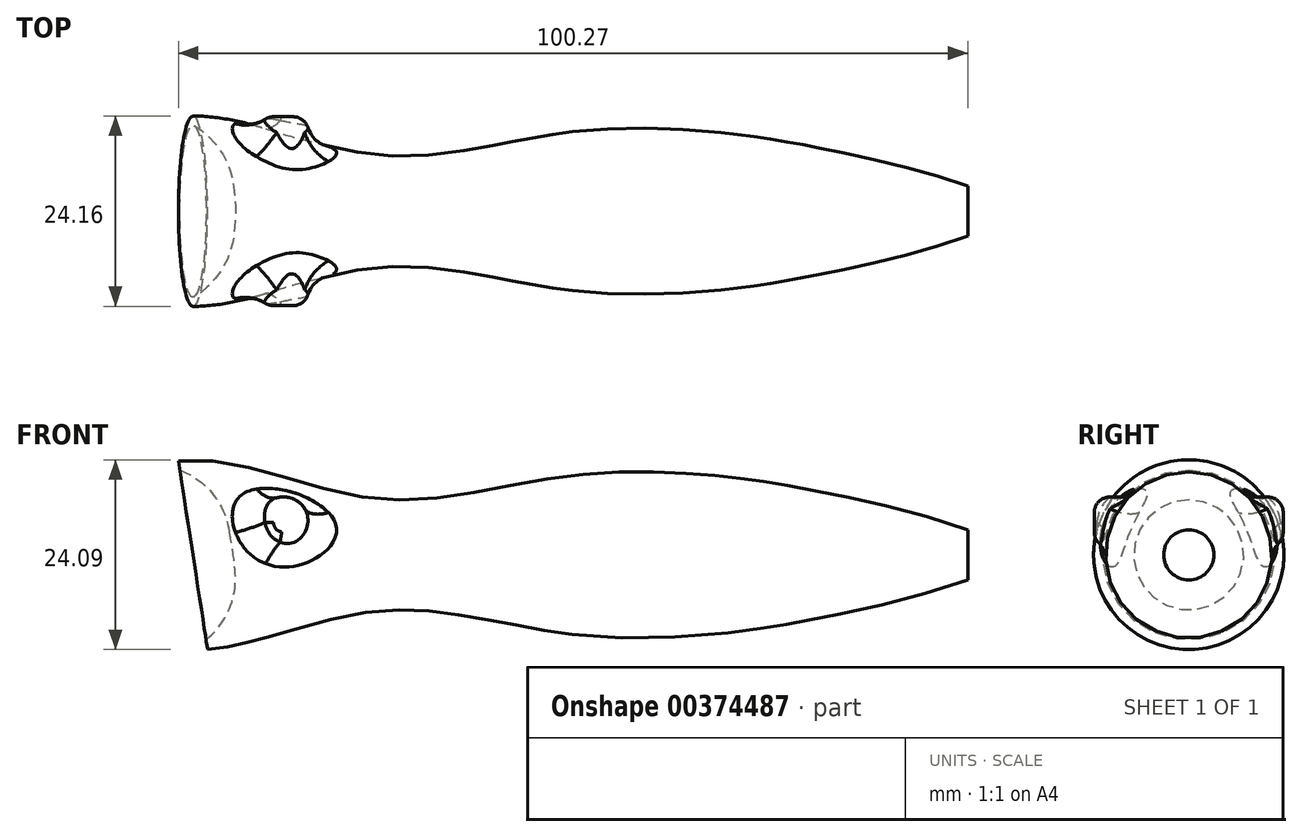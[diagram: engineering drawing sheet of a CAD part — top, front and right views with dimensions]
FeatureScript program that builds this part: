
annotation { "Feature Type Name" : "Feature", "Feature Type Description" : "" }
export const myFeature = defineFeature(function(context is Context, id is Id, definition is map)
    precondition{}
    {
        {
            var Q0;
            Q0=qCreatedBy(makeId("Front.planeOp"),FACE);
            var sketch = newSketch(context, id + "F0", { "sketchPlane" : qUnion([Q0])});
            skLineSegment(sketch, "E0", {"start": v(-64.17, 0) * mm, "end": v(44.05, 0) * mm});
            skFitSpline(sketch, "E1", {"points": [v(-64.13, 11.91) * mm, v(-39.28, 7.2) * mm, v(-14.5, 10.01) * mm, v(5.16, 9.98) * mm, v(16.36, 8.27) * mm, v(44.05, 0) * mm], "startDerivative": vector(102.28, 15.68) * mm, "endDerivative": vector(118.61, -59.18) * mm});
            skLineSegment(sketch, "E2.bottom", {"start": v(36.42, 9.8) * mm, "end": v(56.27, 9.8) * mm});
            skLineSegment(sketch, "E2.top", {"start": v(36.42, -4.91) * mm, "end": v(56.27, -4.91) * mm});
            skLineSegment(sketch, "E2.left", {"start": v(36.42, 9.8) * mm, "end": v(36.42, -4.91) * mm});
            skLineSegment(sketch, "E2.right", {"start": v(56.27, 9.8) * mm, "end": v(56.27, -4.91) * mm});
            skLineSegment(sketch, "E3", {"start": v(-64.13, 11.91) * mm, "end": v(-64.17, 0) * mm});
            skSolve(sketch);
        }
        {
            var Q0;
            {var subQ0=sQuery(id+"F0.wireOp",EDGE,"E3");Q0=makeQuery(id+"F0.imprint","IMPRINT",FACE,{"disambiguationData":[TD([[makeQuery(id+"F0.imprint","IMPRINT",EDGE,{"derivedFrom":subQ0}),1.0]])]});}
            var Q1;
            Q1=sQuery(id+"F0.wireOp",EDGE,"E0");
            revolve(context, id + "F1", {"entities" : qUnion([Q0]), "axis" : qUnion([Q1]), "revolveType" : RevolveType.FULL});
        }
        {
            var Q0;
            Q0=qCreatedBy(makeId("Front.planeOp"),FACE);
            var sketch = newSketch(context, id + "F2", { "sketchPlane" : qUnion([Q0])});
            skLineSegment(sketch, "E4", {"start": v(-65.45, 22.3) * mm, "end": v(-56.64, -34.7) * mm});
            skLineSegment(sketch, "E5", {"start": v(-56.64, -34.7) * mm, "end": v(-81.8, -34.7) * mm});
            skLineSegment(sketch, "E6", {"start": v(-81.8, -34.7) * mm, "end": v(-65.45, 22.3) * mm});
            skSolve(sketch);
        }
        {
            var Q0;
            Q0=makeQuery(id+"F2.imprint","IMPRINT",FACE,{"disambiguationData":[TD([[makeQuery(id+"F2.imprint","IMPRINT",EDGE,{"derivedFrom":sQuery(id+"F2.wireOp",EDGE,"E4")}),-1.0]])]});
            extrude(context, id + "F3", {"entities" : qUnion([Q0]), "operationType" : NewBodyOperationType.REMOVE, "endBound" : BoundingType.SYMMETRIC, "oppositeDirection" : true, "depth" : 32.6 * mm});
        }
        {
            var Q0;
            Q0=makeQuery(id+"F3.boolean.opBoolean","COPY",FACE,{"derivedFrom":makeQuery(id+"F3.opExtrude","SWEPT_FACE",FACE,{"disambiguationData":[OSD([sQuery(id+"F2.wireOp",EDGE,"E4")])]})});
            var sketch = newSketch(context, id + "F4", { "sketchPlane" : qUnion([Q0])});
            skCircle(sketch, "E7", {"center": v(0, 9.47) * mm, "radius": 10.92 * mm});
            skSolve(sketch);
        }
        {
            var Q0;
            Q0 = qSketchRegion(id + "F4", true);
            extrude(context, id + "F5", {"entities" : qUnion([Q0]), "operationType" : NewBodyOperationType.REMOVE, "oppositeDirection" : true, "depth" : 5 * mm});
        }
        {
            var Q0;
            Q0=makeQuery(id+"F5.boolean.opBoolean","COPY",EDGE,{"derivedFrom":makeQuery(id+"F5.opExtrude","CAP_EDGE",EDGE,{"disambiguationData":[OSD([sQuery(id+"F4.wireOp",EDGE,"E7")])],"isStart":false})});
            fillet(context, id + "F6", {"entities" : qUnion([Q0]), "radius" : 10 * mm, "tangentPropagation" : true, "allowEdgeOverflow" : false});
        }
        {
            var Q0;
            Q0=qCreatedBy(makeId("Front.planeOp"),FACE);
            var sketch = newSketch(context, id + "F7", { "sketchPlane" : qUnion([Q0])});
            skCircle(sketch, "E8", {"center": v(-50.52, 4.14) * mm, "radius": 3.23 * mm});
            skSolve(sketch);
        }
        {
            var Q0;
            Q0 = qSketchRegion(id + "F7", true);
            extrude(context, id + "F8", {"entities" : qUnion([Q0]), "operationType" : NewBodyOperationType.ADD, "endBound" : BoundingType.SYMMETRIC, "oppositeDirection" : true, "depth" : 24 * mm});
        }
        {
            var Q0;
            Q0=makeQuery(id+"F8.opExtrude","CAP_EDGE",EDGE,{"disambiguationData":[OSD([sQuery(id+"F7.wireOp",EDGE,"E8")])],"isStart":true});
            var Q1;
            Q1=makeQuery(id+"F8.opExtrude","CAP_EDGE",EDGE,{"disambiguationData":[OSD([sQuery(id+"F7.wireOp",EDGE,"E8")])],"isStart":false});
            fillet(context, id + "F9", {"entities" : qUnion([Q0, Q1]), "radius" : 2 * mm, "tangentPropagation" : true, "allowEdgeOverflow" : false});
        }
        {
            var Q0;
            Q0=makeQuery(id+"F8.boolean.opBoolean","INTERSECT",EDGE,{"disambiguationData":[OD(0.0)],"derivedFrom":[makeQuery(id+"F1.opRevolve","SWEPT_FACE",FACE,{"disambiguationData":[OSD([sQuery(id+"F0.wireOp",EDGE,"E1")])]}),makeQuery(id+"F8.opExtrude","SWEPT_FACE",FACE,{"disambiguationData":[OSD([sQuery(id+"F7.wireOp",EDGE,"E8")])]})]});
            var Q1;
            Q1=makeQuery(id+"F8.boolean.opBoolean","INTERSECT",EDGE,{"disambiguationData":[OD(1.0)],"derivedFrom":[makeQuery(id+"F1.opRevolve","SWEPT_FACE",FACE,{"disambiguationData":[OSD([sQuery(id+"F0.wireOp",EDGE,"E1")])]}),makeQuery(id+"F8.opExtrude","SWEPT_FACE",FACE,{"disambiguationData":[OSD([sQuery(id+"F7.wireOp",EDGE,"E8")])]})]});
            fillet(context, id + "F10", {"entities" : qUnion([Q0, Q1]), "radius" : 5 * mm, "tangentPropagation" : true, "allowEdgeOverflow" : false});
        }
    });
